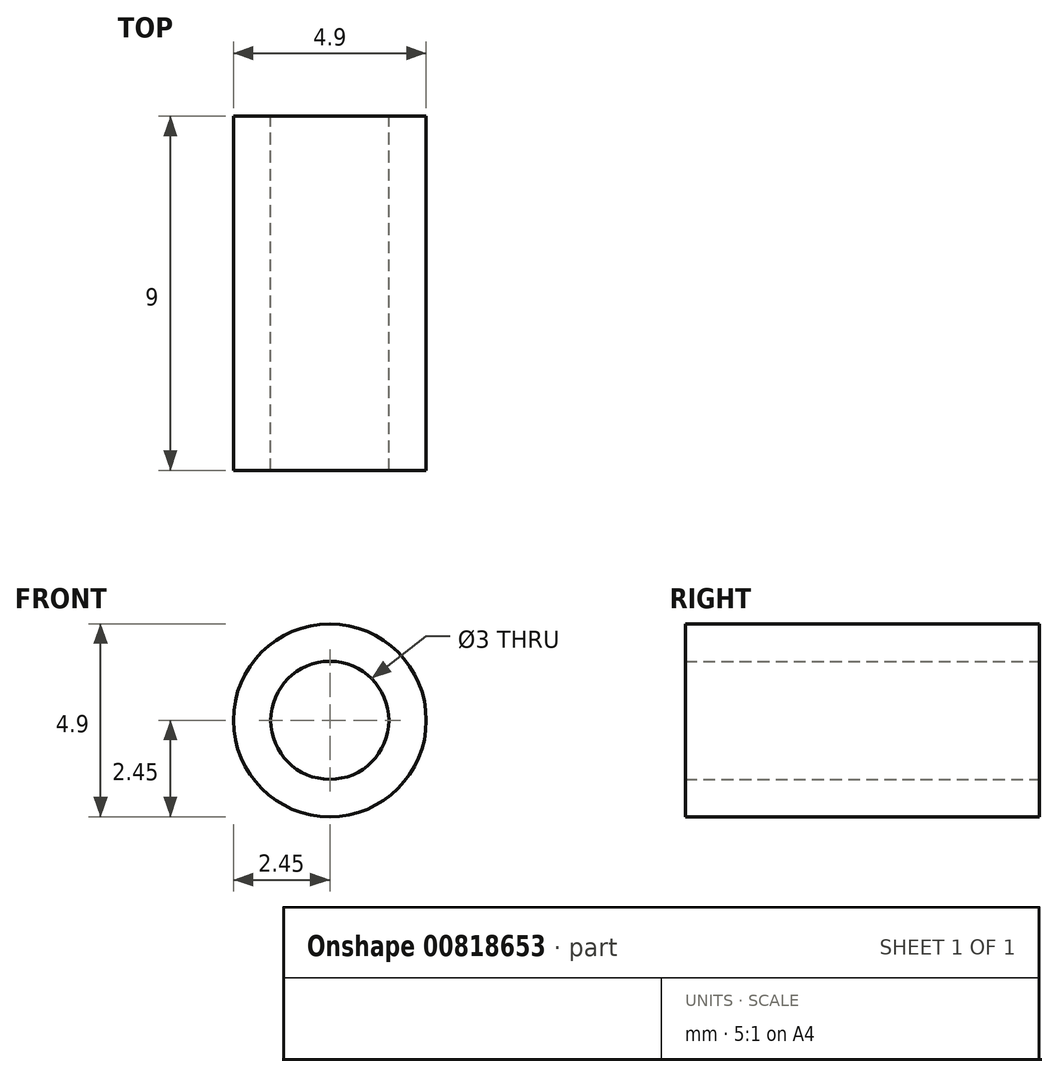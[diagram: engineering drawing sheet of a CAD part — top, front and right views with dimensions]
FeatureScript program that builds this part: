
annotation { "Feature Type Name" : "Feature", "Feature Type Description" : "" }
export const myFeature = defineFeature(function(context is Context, id is Id, definition is map)
    precondition{}
    {
        {
            var Q0;
            Q0=qCreatedBy(makeId("Front.planeOp"),FACE);
            var sketch = newSketch(context, id + "F0", { "sketchPlane" : qUnion([Q0])});
            skCircle(sketch, "E0", {"center": v(0, 0) * mm, "radius": 2.45 * mm});
            skCircle(sketch, "E1", {"center": v(0, 0) * mm, "radius": 1.5 * mm});
            skSolve(sketch);
        }
        {
            var Q0;
            Q0 = qSketchRegion(id + "F0", true);
            extrude(context, id + "F1", {"entities" : qUnion([Q0]), "depth" : 9 * mm, "offsetDistance" : 25 * mm});
        }
    });
